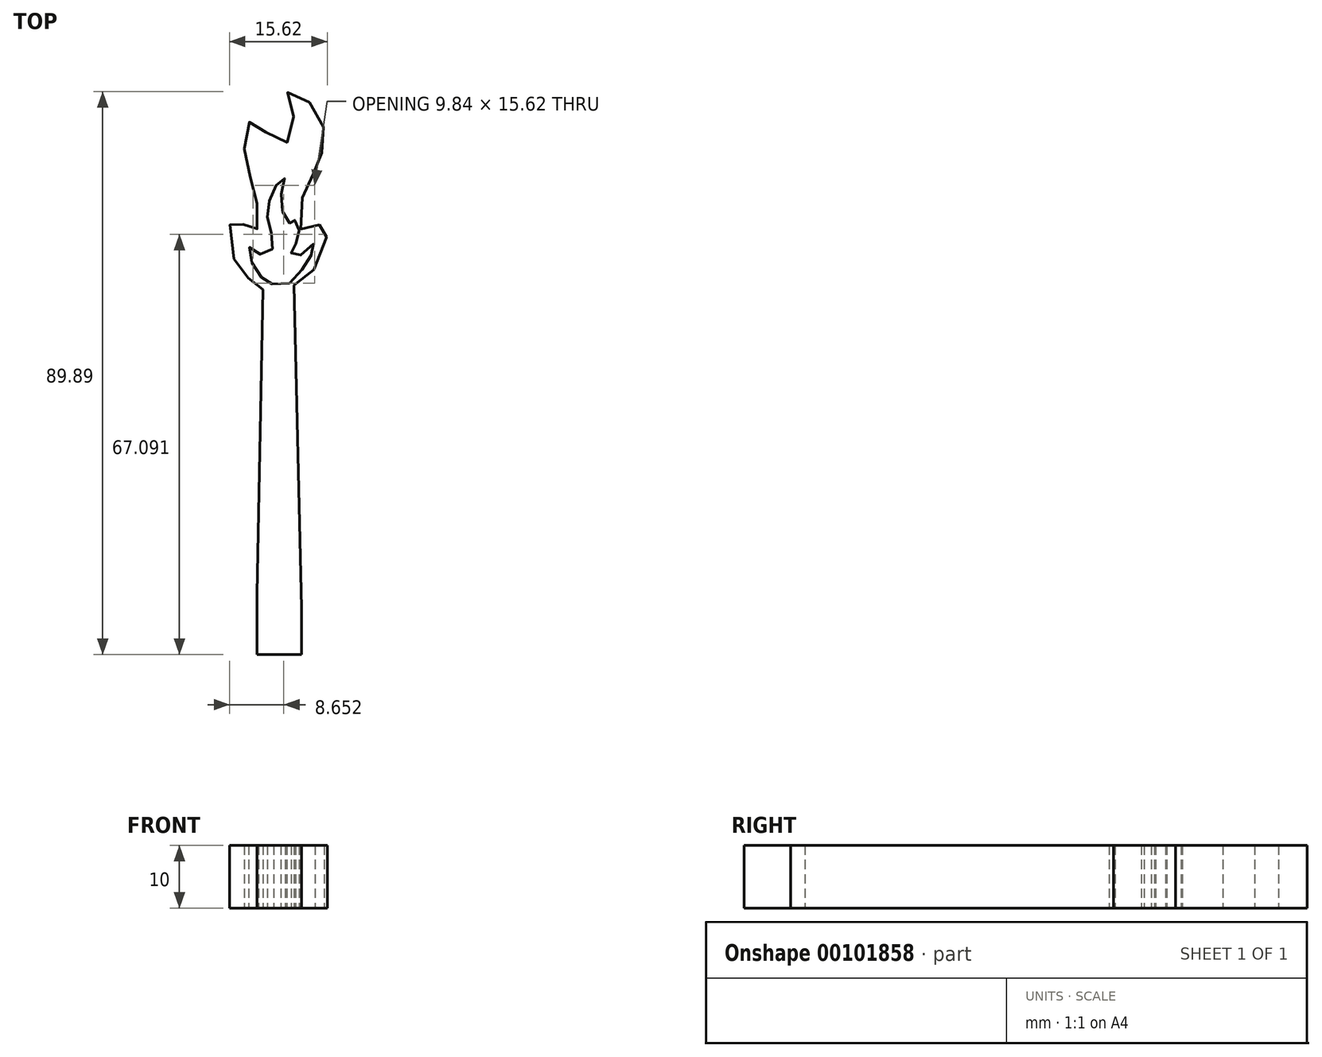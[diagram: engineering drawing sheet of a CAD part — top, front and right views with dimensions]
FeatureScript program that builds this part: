
annotation { "Feature Type Name" : "Feature", "Feature Type Description" : "" }
export const myFeature = defineFeature(function(context is Context, id is Id, definition is map)
    precondition{}
    {
        {
            var Q0;
            Q0=qCreatedBy(makeId("Top.planeOp"),FACE);
            var sketch = newSketch(context, id + "F0", { "sketchPlane" : qUnion([Q0])});
            skFitSpline(sketch, "E0", {"points": [v(2.5, 46.16) * mm, v(6.4, 49.86) * mm, v(7.47, 56.05) * mm, v(4.11, 54.64) * mm, v(3.95, 60.47) * mm, v(6.07, 64.7) * mm, v(7.32, 69.3) * mm, v(5.74, 74.6) * mm, v(1.5, 76.91) * mm, v(2.73, 71.26) * mm, v(0, 68.79) * mm, v(-3.99, 72.5) * mm, v(-5.4, 68.8) * mm, v(-4.18, 62.43) * mm, v(-3.13, 56.95) * mm, v(-4.02, 54.48) * mm, v(-7.02, 56.96) * mm, v(-7.2, 50.77) * mm, v(-4.56, 47.06) * mm, v(-2.45, 45.46) * mm, v(2.5, 46.16) * mm]});
            skLineSegment(sketch, "E1", {"start": v(-2.45, 45.46) * mm, "end": v(-3.35, -3.12) * mm});
            skLineSegment(sketch, "E2", {"start": v(2.5, 46.16) * mm, "end": v(3.72, -5.42) * mm});
            skLineSegment(sketch, "E3", {"start": v(-3.35, -3.12) * mm, "end": v(-3.35, -12.84) * mm});
            skLineSegment(sketch, "E4", {"start": v(-3.35, -12.84) * mm, "end": v(3.72, -12.84) * mm});
            skLineSegment(sketch, "E5", {"start": v(3.72, -12.84) * mm, "end": v(3.72, -5.42) * mm});
            skFitSpline(sketch, "E6", {"points": [v(1.85, 46.44) * mm, v(3.3, 47.95) * mm, v(4.68, 49.67) * mm, v(5.48, 51.36) * mm, v(5.87, 52.85) * mm, v(4.9, 51.93) * mm, v(3.56, 50.9) * mm, v(2.66, 50.6) * mm, v(2.1, 51.27) * mm, v(2.45, 52.7) * mm, v(2.68, 52.69) * mm, v(3.53, 53.85) * mm, v(3.4, 54.82) * mm, v(2.76, 55.44) * mm, v(2.77, 56.01) * mm, v(2.34, 57.15) * mm, v(2, 56.17) * mm, v(1.43, 56.27) * mm, v(0.78, 57.73) * mm, v(0.45, 59.52) * mm, v(0.6, 61.6) * mm, v(0.99, 63.05) * mm, v(1.09, 63.6) * mm, v(-0.56, 61.72) * mm, v(-1.2, 60.3) * mm, v(-1.7, 58.1) * mm, v(-1.67, 56.84) * mm, v(-1.38, 55.25) * mm, v(-0.75, 53.55) * mm, v(-0.99, 51.8) * mm, v(-2.04, 51.11) * mm, v(-3.26, 51.18) * mm, v(-4.2, 51.93) * mm, v(-4.68, 52.15) * mm, v(-4.42, 50.44) * mm, v(-3.53, 48.62) * mm, v(-2.3, 46.96) * mm, v(-1.57, 46.4) * mm, v(-0.39, 46.37) * mm, v(1.85, 46.44) * mm]});
            skSolve(sketch);
        }
        {
            var Q0;
            Q0=makeQuery(id+"F0.imprint","IMPRINT",FACE,{"disambiguationData":[TD([[makeQuery(id+"F0.imprint","IMPRINT",EDGE,{"derivedFrom":sQuery(id+"F0.wireOp",EDGE,"E6")}),-1.0]])]});
            var Q1;
            {var subQ0=sQuery(id+"F0.wireOp",EDGE,"E1");Q1=makeQuery(id+"F0.imprint","IMPRINT",FACE,{"disambiguationData":[TD([[makeQuery(id+"F0.imprint","IMPRINT",EDGE,{"derivedFrom":subQ0}),1.0]])]});}
            extrude(context, id + "F1", {"entities" : qUnion([Q0, Q1]), "depth" : 10 * mm});
        }
    });
